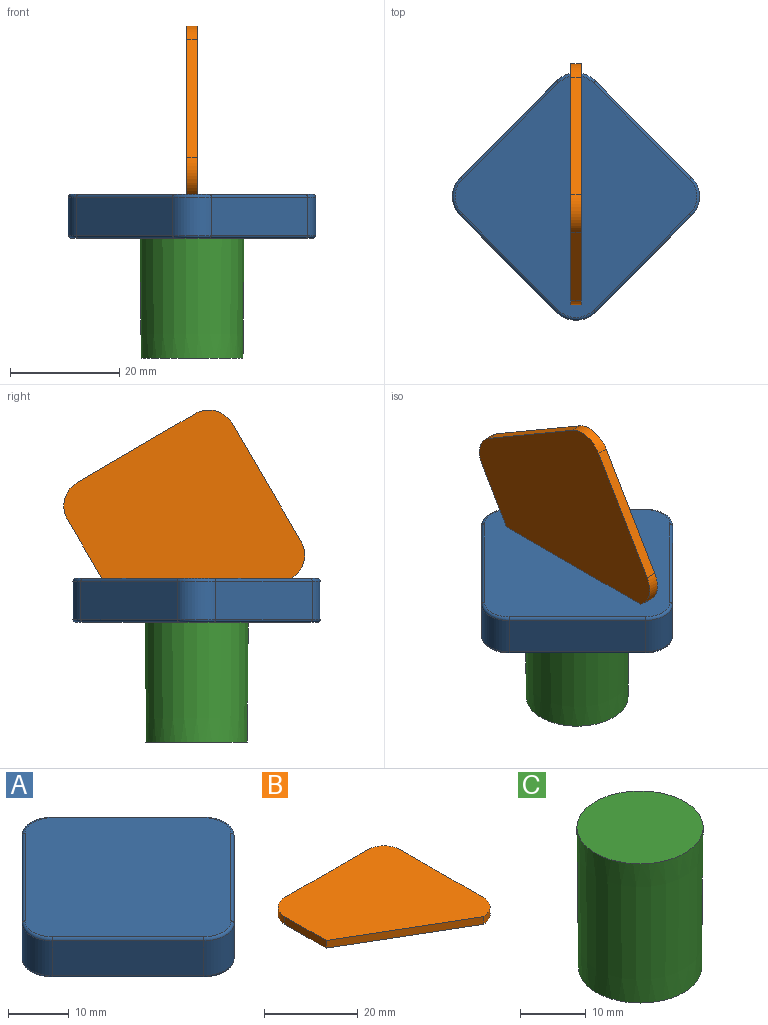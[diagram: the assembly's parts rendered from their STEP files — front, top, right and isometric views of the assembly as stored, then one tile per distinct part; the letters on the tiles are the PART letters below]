
ASSEMBLY  parts=3 mates=2
PART A: 28 faces, bbox 46.2x46.2x8 mm
  f0: plane 17.68x17.68mm, normal (0.71,-0.71,0), area 175mm2, adj f1,f7,f19,f23
  f1: cylinder r=5mm len=7.07mm, axis (0,0,-1), area 55mm2, adj f0,f2,f18,f21
  f2: plane 17.68x17.68mm, normal (0.71,0.71,0), area 175mm2, adj f1,f3,f16,f20
  f3: cylinder r=5mm len=7.07mm, axis (0,0,-1), area 55mm2, adj f2,f4,f14,f22
  f4: plane 17.68x17.68mm, normal (-0.71,0.71,0), area 175mm2, adj f3,f5,f12,f24
  f5: cylinder r=5mm len=7.07mm, axis (0,0,-1), area 55mm2, adj f4,f6,f13,f26
  f6: plane 17.68x17.68mm, normal (-0.71,-0.71,0), area 175mm2, adj f5,f7,f15,f27
  f7: cylinder r=5mm len=7.07mm, axis (0,0,-1), area 55mm2, adj f0,f6,f17,f25
  f8: plane 44.36x44.36mm, normal (0,0,1), area 1138.6mm2, adj f20,f21,f22,f23,f24,f25,f26,f27
  f9: cylinder r=9.35mm len=18.7mm, axis (0,0,1), area 235mm2, adj f10,f11
  f10: plane 44.36x44.36mm, normal (0,0,-1), area 864mm2, adj f9,f12,f13,f14,f15,f16,f17,f18
  f11: plane 18.7x18.7mm, normal (0,0,-1), area 274.6mm2, adj f9
  f12: cylinder r=0.5mm len=18.03mm, axis (-0.71,-0.71,0), area 19.6mm2, adj f4,f10,f13,f14
  f13: torus R=4.5mm, axis (0,0,1), area 5.9mm2, adj f5,f10,f12,f15
  f14: torus R=4.5mm, axis (0,0,1), area 5.9mm2, adj f3,f10,f12,f16
  f15: cylinder r=0.5mm len=18.03mm, axis (0.71,-0.71,0), area 19.6mm2, adj f6,f10,f13,f17
  f16: cylinder r=0.5mm len=18.03mm, axis (-0.71,0.71,0), area 19.6mm2, adj f2,f10,f14,f18
  f17: torus R=4.5mm, axis (0,0,1), area 5.9mm2, adj f7,f10,f15,f19
  f18: torus R=4.5mm, axis (0,0,1), area 5.9mm2, adj f1,f10,f16,f19
  f19: cylinder r=0.5mm len=18.03mm, axis (0.71,0.71,0), area 19.6mm2, adj f0,f10,f17,f18
  f20: cylinder r=0.5mm len=18.03mm, axis (0.71,-0.71,0), area 19.6mm2, adj f2,f8,f21,f22
  f21: torus R=4.5mm, axis (0,0,1), area 5.9mm2, adj f1,f8,f20,f23
  f22: torus R=4.5mm, axis (0,0,1), area 5.9mm2, adj f3,f8,f20,f24
  f23: cylinder r=0.5mm len=18.03mm, axis (-0.71,-0.71,0), area 19.6mm2, adj f0,f8,f21,f25
  f24: cylinder r=0.5mm len=18.03mm, axis (0.71,0.71,0), area 19.6mm2, adj f4,f8,f22,f26
  f25: torus R=4.5mm, axis (0,0,1), area 5.9mm2, adj f7,f8,f23,f27
  f26: torus R=4.5mm, axis (0,0,1), area 5.9mm2, adj f5,f8,f24,f27
  f27: cylinder r=0.5mm len=18.03mm, axis (-0.71,0.71,0), area 19.6mm2, adj f6,f8,f25,f26
PART B: 9 faces, bbox 35x35x2 mm
  f0: plane 25x2mm, normal (0,1,0), area 50mm2, adj f1,f6,f7,f8
  f1: cylinder r=5mm len=5mm, axis (0,0,-1), area 15.7mm2, adj f0,f2,f7,f8
  f2: plane 12.5x2mm, normal (-1,0,0), area 25mm2, adj f1,f3,f7,f8
  f3: plane 30x17.5mm, normal (-0.5,-0.86,0), area 69.5mm2, adj f2,f4,f7,f8
  f4: cylinder r=5mm len=5mm, axis (0,0,-1), area 15.7mm2, adj f3,f5,f7,f8
  f5: plane 25x2mm, normal (1,0,0), area 50mm2, adj f4,f6,f7,f8
  f6: cylinder r=5mm len=5mm, axis (0,0,-1), area 15.7mm2, adj f0,f5,f7,f8
  f7: plane 35x35mm, normal (0,0,1), area 946.4mm2, adj f0,f1,f2,f3,f4,f5,f6
  f8: plane 35x35mm, normal (0,0,-1), area 946.4mm2, adj f0,f1,f2,f3,f4,f5,f6
PART C: 3 faces, bbox 19.2x19.2x26 mm
  f0: cone r=9.35mm half-angle=0.5deg, axis (0,0,1), area 1546mm2, adj f1,f2
  f1: plane 19.15x19.15mm, normal (0,0,1), area 288.1mm2, adj f0
  f2: plane 18.7x18.7mm, normal (0,0,-1), area 274.6mm2, adj f0
PLACE A t=(-28.86,-10.16,-15.7)mm
PLACE B rot(axis=(0.45,-0.78,-0.45),104.4deg) t=(-27.86,-7.91,-2.89)mm
PLACE C t=(-28.86,-10.16,-41.7)mm
MATE fastened B.f3 <-> A.f9  axis (0,0,-1) through (-28.86,-10.16,-11.7)mm
MATE fastened C.f0 <-> A.f9  axis (0,0,1) through (-28.86,-10.16,-15.7)mm
